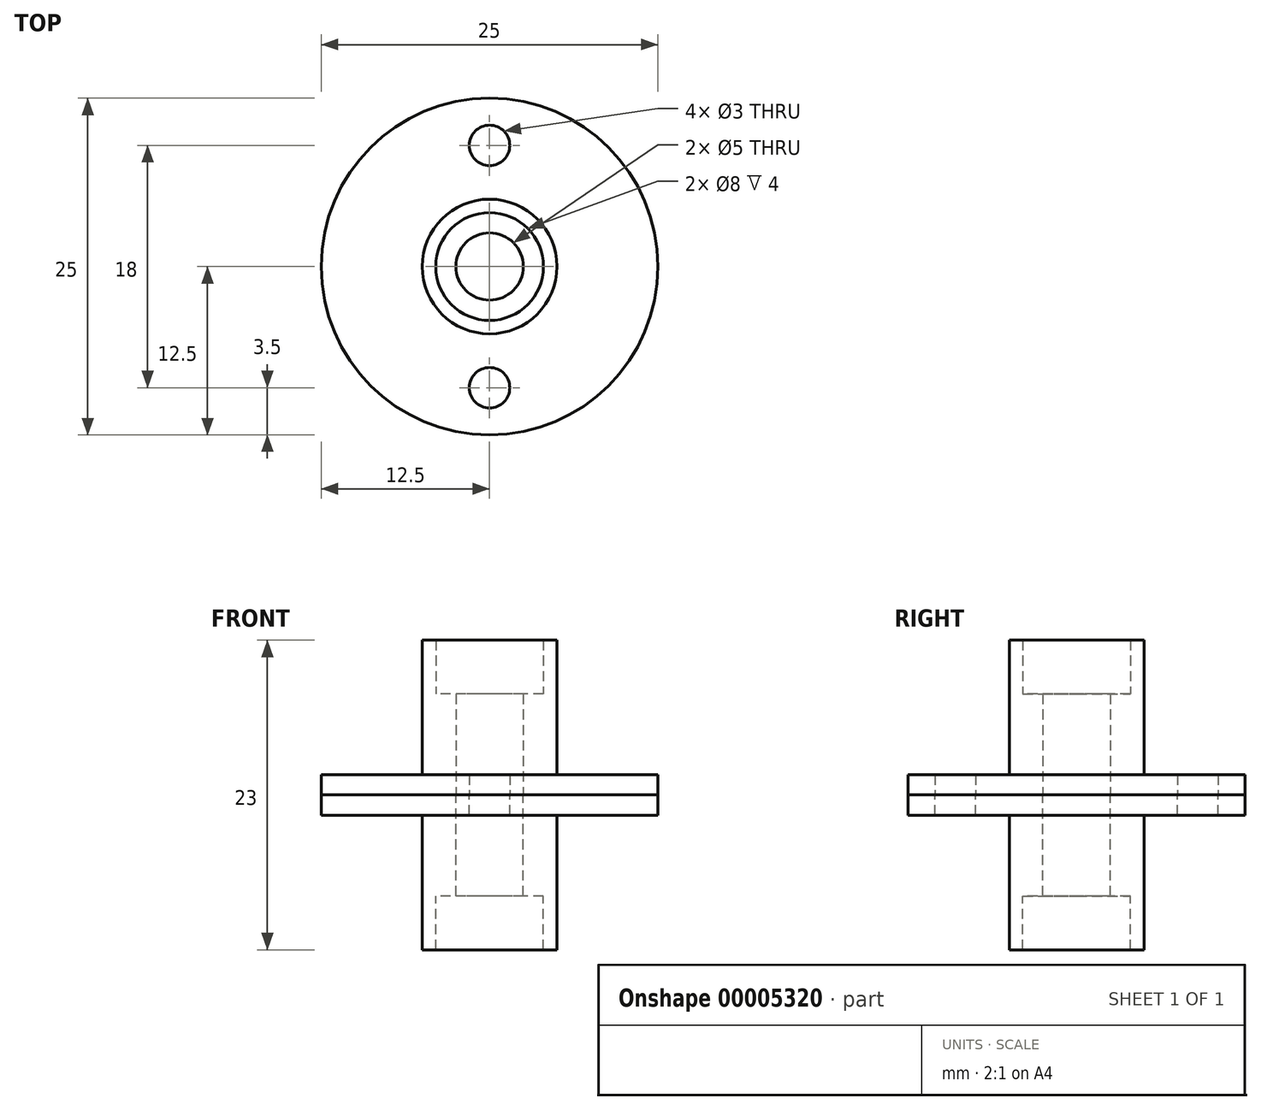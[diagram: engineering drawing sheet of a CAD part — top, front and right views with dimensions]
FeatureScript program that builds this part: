
annotation { "Feature Type Name" : "Feature", "Feature Type Description" : "" }
export const myFeature = defineFeature(function(context is Context, id is Id, definition is map)
    precondition{}
    {
        {
            var Q0;
            Q0=qCreatedBy(makeId("Top.planeOp"),FACE);
            var sketch = newSketch(context, id + "F0", { "sketchPlane" : qUnion([Q0])});
            skCircle(sketch, "E0", {"center": v(0, 0) * mm, "radius": 2.5 * mm});
            skCircle(sketch, "E1", {"center": v(0, 0) * mm, "radius": 4 * mm});
            skCircle(sketch, "E2", {"center": v(0, 0) * mm, "radius": 5 * mm});
            skCircle(sketch, "E3", {"center": v(0, 0) * mm, "radius": 12.5 * mm});
            skCircle(sketch, "E4", {"center": v(0, 9) * mm, "radius": 1.5 * mm});
            skCircle(sketch, "E5", {"center": v(0, -9) * mm, "radius": 1.5 * mm});
            skSolve(sketch);
        }
        {
            var Q0;
            Q0=makeQuery(id+"F0.imprint","IMPRINT",FACE,{"disambiguationData":[TD([[makeQuery(id+"F0.imprint","IMPRINT",EDGE,{"derivedFrom":sQuery(id+"F0.wireOp",EDGE,"E0")}),-1.0]])]});
            extrude(context, id + "F1", {"entities" : qUnion([Q0]), "depth" : 7.5 * mm});
        }
        {
            var Q0;
            Q0=makeQuery(id+"F0.imprint","IMPRINT",FACE,{"disambiguationData":[TD([[makeQuery(id+"F0.imprint","IMPRINT",EDGE,{"derivedFrom":sQuery(id+"F0.wireOp",EDGE,"E1")}),-1.0]])]});
            extrude(context, id + "F2", {"entities" : qUnion([Q0]), "operationType" : NewBodyOperationType.ADD, "depth" : 11.5 * mm});
        }
        {
            var Q0;
            Q0=makeQuery(id+"F0.imprint","IMPRINT",FACE,{"disambiguationData":[TD([[makeQuery(id+"F0.imprint","IMPRINT",EDGE,{"derivedFrom":sQuery(id+"F0.wireOp",EDGE,"E2")}),-1.0]])]});
            extrude(context, id + "F3", {"entities" : qUnion([Q0]), "operationType" : NewBodyOperationType.ADD, "depth" : 1.5 * mm});
        }
        {
            var Q0;
            Q0=makeQuery(id+"F1.opExtrude","SWEPT_BODY",BODY,{"disambiguationData":[OSD([sQuery(id+"F0.wireOp",EDGE,"E0"),sQuery(id+"F0.wireOp",EDGE,"E1")])]});
            var Q1;
            Q1=qCreatedBy(makeId("Top.planeOp"),FACE);
            mirror(context, id + "F4", {"entities" : qUnion([Q0]), "mirrorPlane" : qUnion([Q1])});
        }
    });
